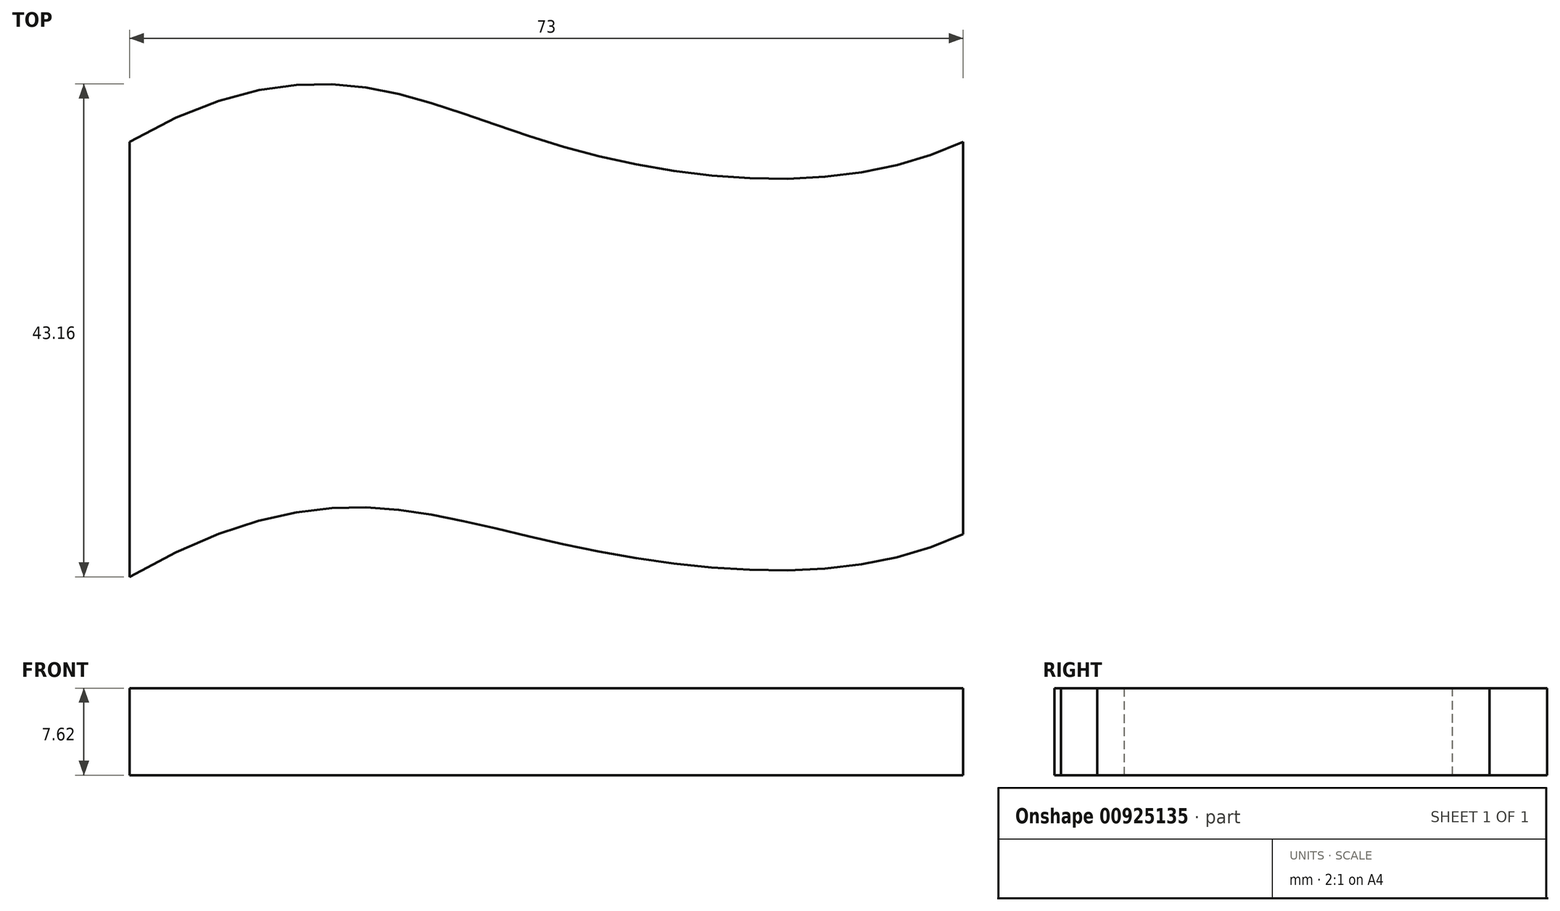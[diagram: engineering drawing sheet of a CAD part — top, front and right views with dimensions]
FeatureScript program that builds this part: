
annotation { "Feature Type Name" : "Feature", "Feature Type Description" : "" }
export const myFeature = defineFeature(function(context is Context, id is Id, definition is map)
    precondition{}
    {
        {
            var Q0;
            Q0=qCreatedBy(makeId("Top.planeOp"),FACE);
            var sketch = newSketch(context, id + "F0", { "sketchPlane" : qUnion([Q0])});
            skLineSegment(sketch, "E0.left", {"start": v(-36.5, 19.05) * mm, "end": v(-36.5, -19.05) * mm});
            skLineSegment(sketch, "E0.right", {"start": v(36.5, 19.05) * mm, "end": v(36.5, -15.32) * mm});
            skPoint(sketch, "E0.middle", {"position": v(0, 0) * mm});
            skPoint(sketch, "E1.start.orphan", {"position": v(0, 19.05) * mm});
            skPoint(sketch, "E2.start.orphan", {"position": v(0, -19.05) * mm});
            skFitSpline(sketch, "E3", {"points": [v(-36.5, 19.05) * mm, v(0, 19.05) * mm, v(36.5, 19.05) * mm], "startDerivative": vector(97.08, 55.9) * mm, "endDerivative": vector(62.99, 30.13) * mm});
            skFitSpline(sketch, "E4", {"points": [v(-36.5, -19.05) * mm, v(0, -15.88) * mm, v(36.5, -15.32) * mm], "startDerivative": vector(97.08, 55.9) * mm, "endDerivative": vector(62.99, 30.13) * mm});
            skPoint(sketch, "E5.orphan", {"position": v(36.5, -19.05) * mm});
            skSolve(sketch);
        }
        {
            var Q0;
            Q0 = qSketchRegion(id + "F0", true);
            extrude(context, id + "F1", {"entities" : qUnion([Q0]), "depth" : 7.62 * mm, "offsetDistance" : 25.4 * mm});
        }
    });
